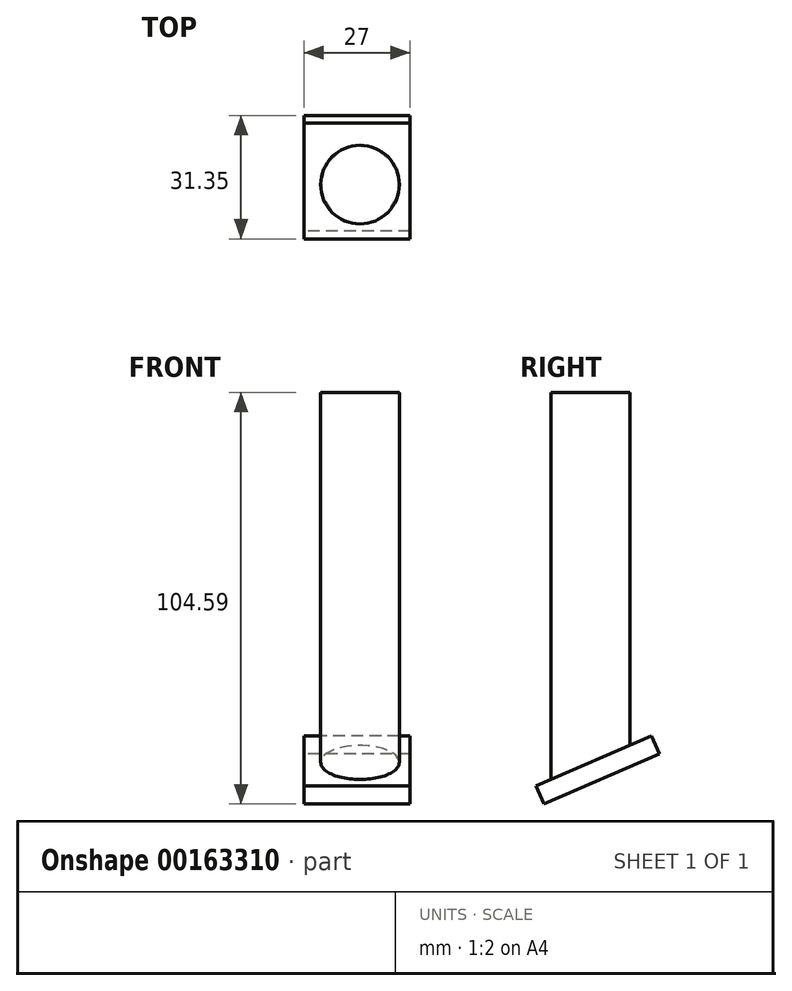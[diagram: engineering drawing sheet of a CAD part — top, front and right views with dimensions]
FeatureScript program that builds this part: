
annotation { "Feature Type Name" : "Feature", "Feature Type Description" : "" }
export const myFeature = defineFeature(function(context is Context, id is Id, definition is map)
    precondition{}
    {
        {
            var Q0;
            Q0=qCreatedBy(makeId("Top.planeOp"),FACE);
            var sketch = newSketch(context, id + "F0", { "sketchPlane" : qUnion([Q0])});
            skCircle(sketch, "E0", {"center": v(-12.75, 13.79) * mm, "radius": 10 * mm});
            skSolve(sketch);
        }
        {
            var Q0;
            Q0 = qSketchRegion(id + "F0", true);
            extrude(context, id + "F1", {"entities" : qUnion([Q0]), "depth" : 100 * mm});
        }
        {
            var Q0;
            Q0=qCreatedBy(makeId("Right.planeOp"),FACE);
            var sketch = newSketch(context, id + "F2", { "sketchPlane" : qUnion([Q0])});
            skLineSegment(sketch, "E1", {"start": v(0, 0) * mm, "end": v(35.48, 0) * mm});
            skLineSegment(sketch, "E2", {"start": v(35.48, 0) * mm, "end": v(35.48, 15.4) * mm});
            skLineSegment(sketch, "E3", {"start": v(35.48, 15.4) * mm, "end": v(0, 0) * mm});
            skSolve(sketch);
        }
        {
            var Q0;
            Q0=makeQuery(id+"F2.imprint","IMPRINT",FACE,{"disambiguationData":[TD([[makeQuery(id+"F2.imprint","IMPRINT",EDGE,{"derivedFrom":sQuery(id+"F2.wireOp",EDGE,"E1")}),1.0]])]});
            extrude(context, id + "F3", {"entities" : qUnion([Q0]), "operationType" : NewBodyOperationType.REMOVE, "oppositeDirection" : true, "depth" : 25 * mm});
        }
        {
            var Q0;
            Q0=makeQuery(id+"F3.boolean.opBoolean","COPY",FACE,{"derivedFrom":makeQuery(id+"F3.opExtrude","SWEPT_FACE",FACE,{"disambiguationData":[OSD([sQuery(id+"F2.wireOp",EDGE,"E3")])]})});
            var sketch = newSketch(context, id + "F4", { "sketchPlane" : qUnion([Q0])});
            skLineSegment(sketch, "E4.bottom", {"start": v(0, 0) * mm, "end": v(-27, 0) * mm});
            skLineSegment(sketch, "E4.top", {"start": v(0, -32) * mm, "end": v(-27, -32) * mm});
            skLineSegment(sketch, "E4.left", {"start": v(0, 0) * mm, "end": v(0, -32) * mm});
            skLineSegment(sketch, "E4.right", {"start": v(-27, 0) * mm, "end": v(-27, -32) * mm});
            skSolve(sketch);
        }
        {
            var Q0;
            Q0 = qSketchRegion(id + "F4", true);
            extrude(context, id + "F5", {"entities" : qUnion([Q0]), "operationType" : NewBodyOperationType.ADD, "depth" : 5 * mm});
        }
    });
